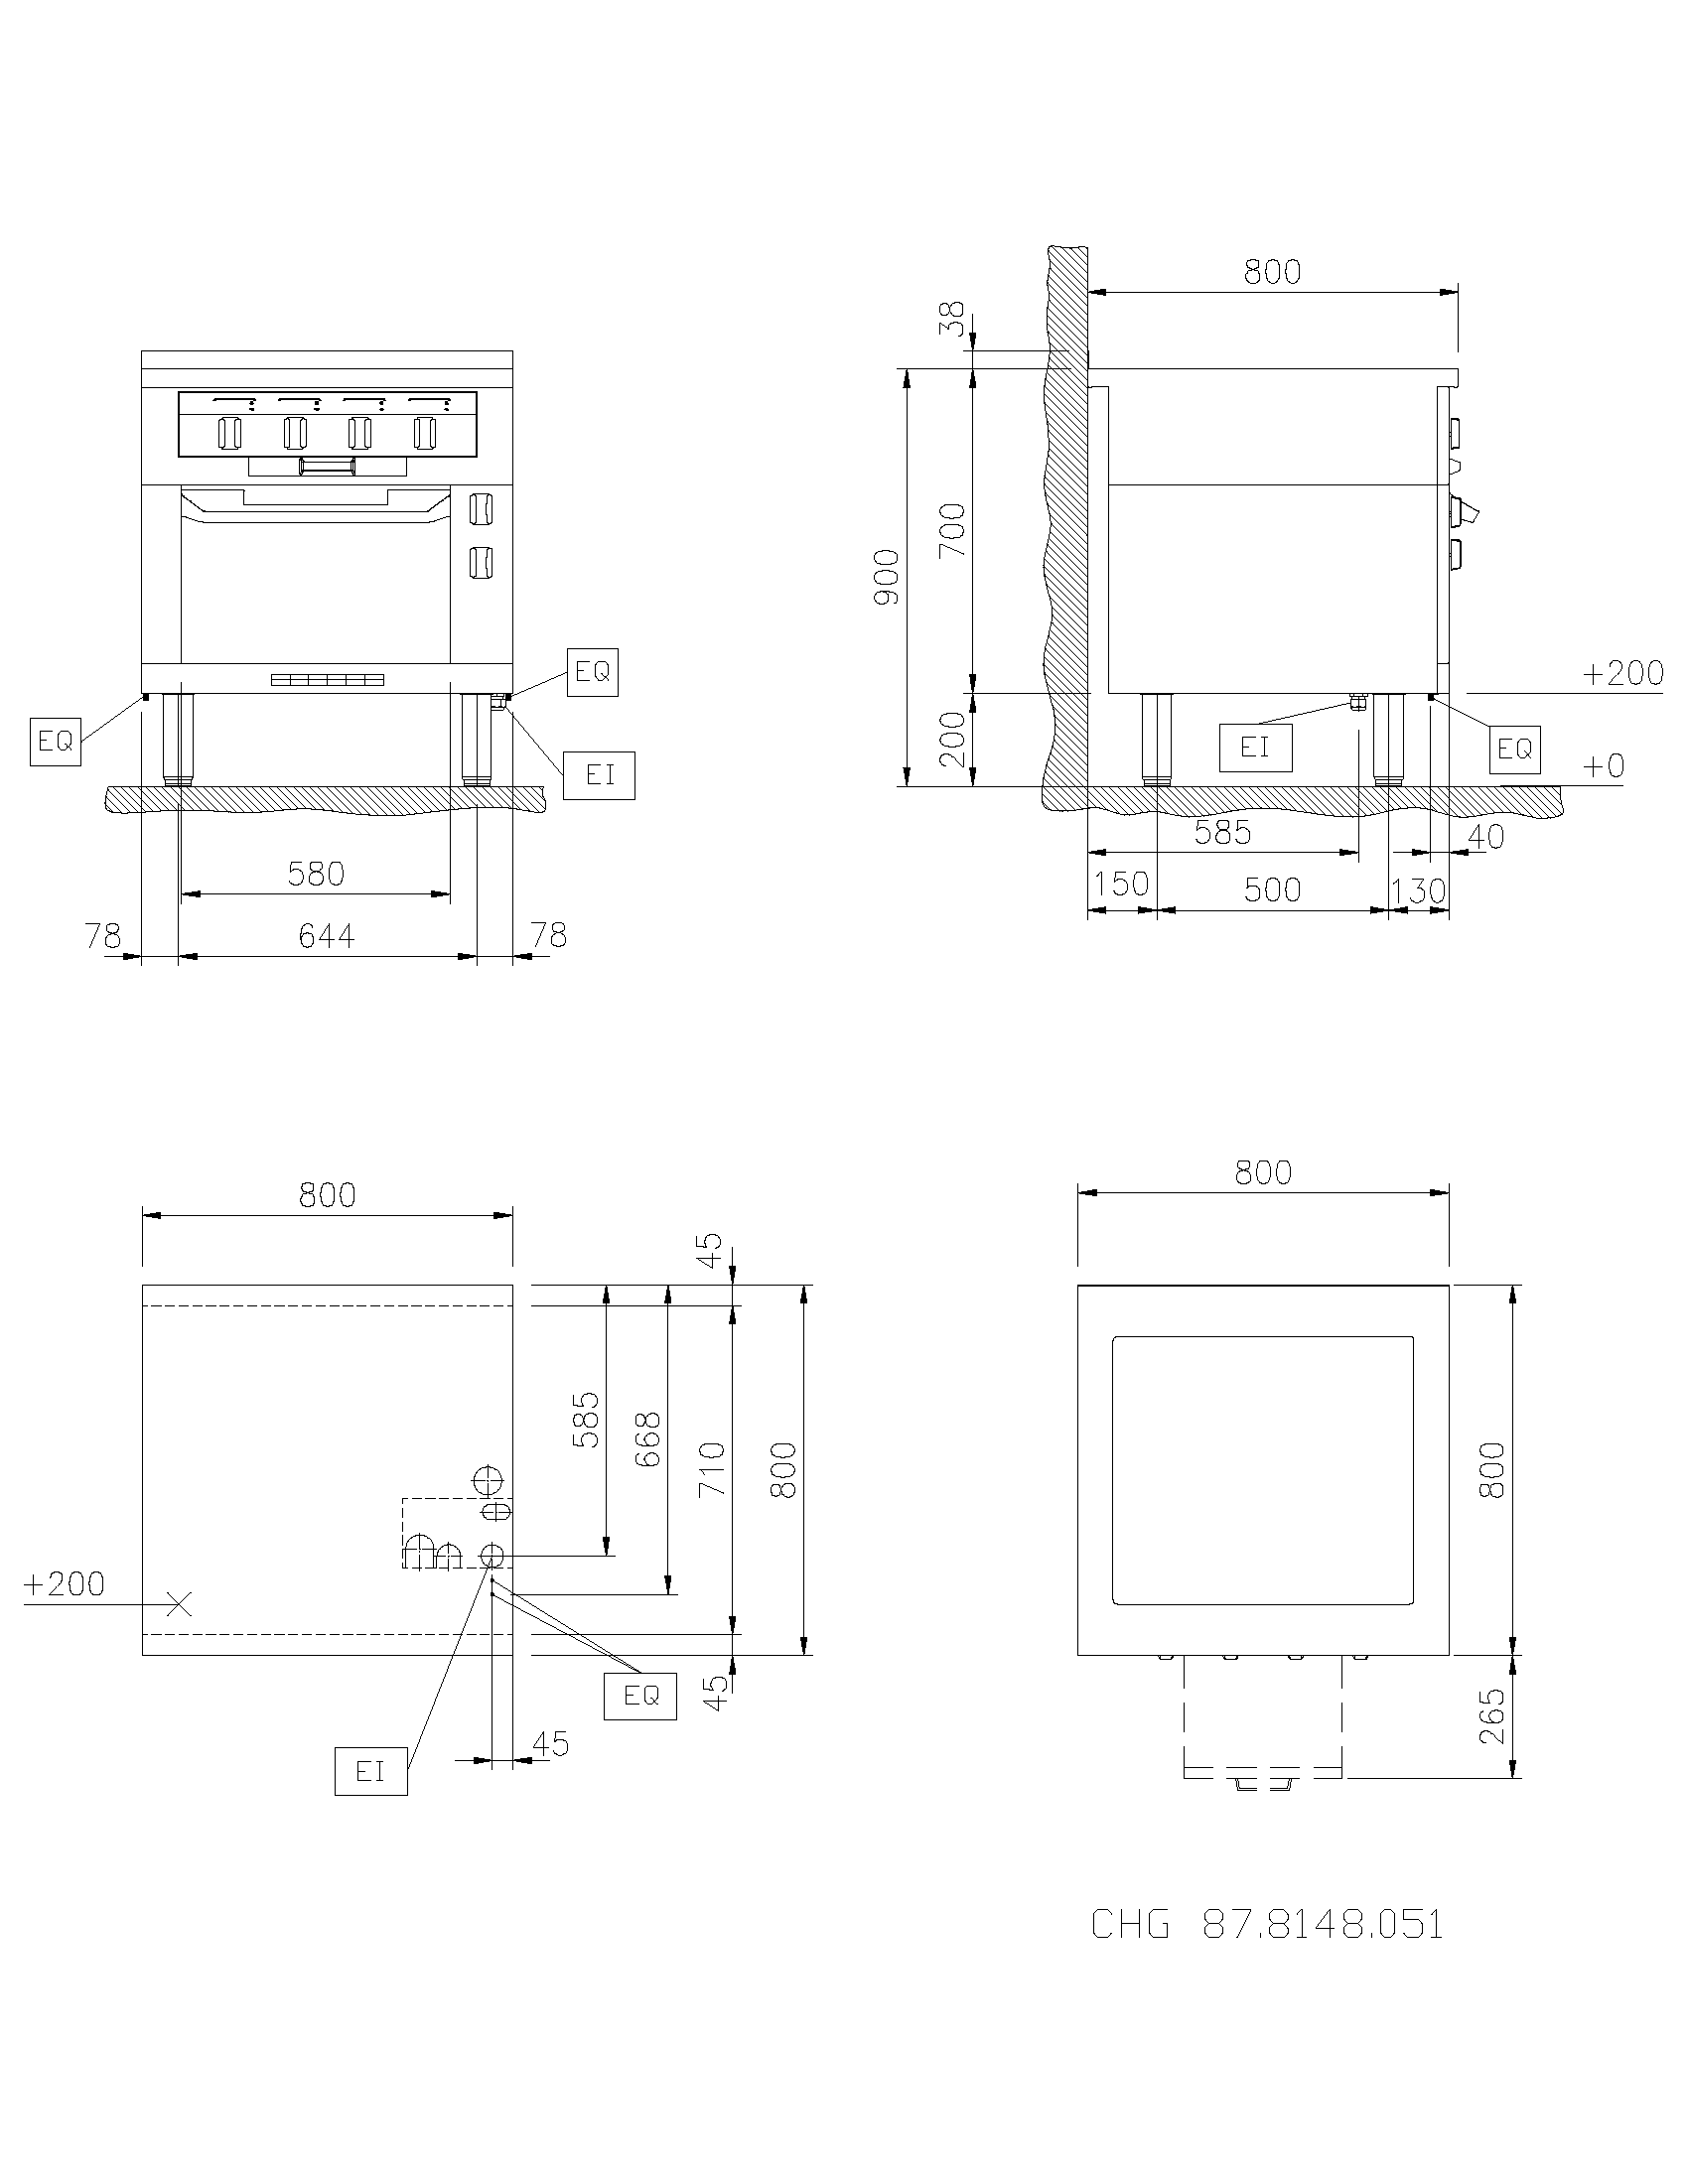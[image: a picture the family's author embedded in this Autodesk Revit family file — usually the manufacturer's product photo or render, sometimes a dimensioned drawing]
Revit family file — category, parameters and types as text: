
# Revit family: QF_ELECTROLUXPROFESSIONAL_588438_MAIRFCH4AO
name_source: partatom
category: Attrezzature speciali
units: mm (PartAtom-declared; Revit-internal decimal feet)

## family parameters
Basato su piano di lavoro = No
Condiviso = No
Punto di calcolo locali = No
Quota connettore circolare = Usa diametro
Sempre verticale = Sì
Taglio con vuoti quando caricato = No
Tipo di parte = Normale

## types (1)
- Standard
    Accessory = Sì
    Cold Water Size = 0"
    Compressed Air Pressure = 0.00 psi
    Compressed Air Size = 0"
    Compressed Air Volume = 0 GPM
    Condensate Return Size = 0"
    Cycle = 50 Hz
    Depth Actual = 800 mm  [stored 2.62467 ft]
    Descrizione = INDUCTION,4Z,WARM CAB PASS,2S,800X800X80
    Direct Waste Size = 0"
    Gas Input Pressure = 0.0
    Gas KW = 0
    Gas Size = 0"
    HP = 29.5 HP
    Height Actual = 800 mm  [stored 2.62467 ft]
    Hot Water Size = 0"
    Item Number = 588438
    Length Actual = 800 mm  [stored 2.62467 ft]
    Modello = MAIRFCH4AO
    Phase = 3
    Produttore = Electrolux Professional
    Prospetto di default = 0 mm  [stored 0 ft]
    Refrigerant Compressor Remote = Sì
    Refrigeration Liquid Line Size = 0 mm  [stored 0 ft]
    Refrigeration Suction Line Size = 0 mm  [stored 0 ft]
    Steam Consumption per Hour = 0
    Steam Supply Maximum Pressure = 0.00 psi
    Steam Supply Minimum Pressure = 0.00 psi
    Steam Supply Size = 0"
    URL = https://www.electroluxprofessional.com
    URL Manufacturer = https://www.electroluxprofessional.com
    Volts = 400 V
    Watts = 22000 W
    Weight = 76.00 kg

note: source unit labels omitted for Gas Input Pressure — the stored unit's dimension contradicts the parameter name (converter mislabeling)

note: [stored X ft] marks values corroborated as IEEE doubles in the binary element streams (Revit-internal decimal feet)

## geometry (parser evidence)
native form markers: Blend x10, Sweep x8
no freeform markers — native parametric forms only
